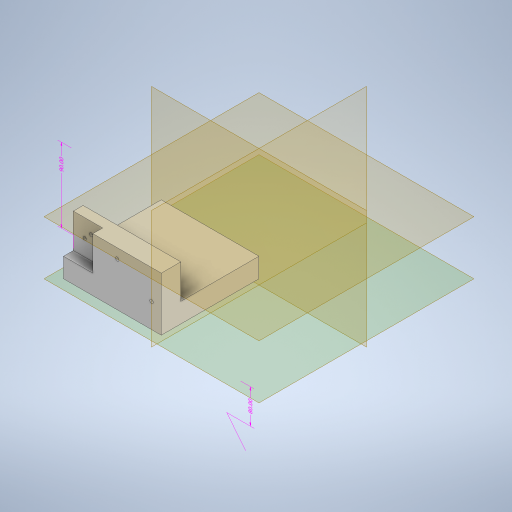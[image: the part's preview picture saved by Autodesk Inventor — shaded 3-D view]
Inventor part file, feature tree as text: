
AUTODESK INVENTOR PART (.ipt)
format: ipt  version: 2023 (Build 270158000, 158)  size: 432,128 bytes
history: native  units: mm
features: sketch x9, extrude x5, other x4, hole x4, plane x4, split x4
ambient origin geometry x8: Origin, YZ Plane, XZ Plane, XY Plane, X Axis, Y Axis, Z Axis, Center Point
bodies: Body1 (feature_tree)
feature tree (30):
  other  "Sólido1"
  other  "Anotaciones"
  extrude  "Extrusión1"  Depth=200.0mm
  hole  "Agujero1"  [1 undecoded]
  extrude  "Extrusión2"  Depth=15.0mm
  extrude  "Extrusión3"  Depth=80.0mm TaperAngle=0.0deg
  extrude  "Extrusión4"  Depth=200.0mm
  extrude  "Extrusión5"  Depth=20.0mm
  hole  "Agujero2"  [1 undecoded]
  plane  "Plano de trabajo1"
  split  "Dividir1"
  plane  "Plano de trabajo2"
  plane  "Plano de trabajo3"
  sketch  "Boceto9"  dims[d37=20.0mm d38=20.0mm]
  plane  "Plano de trabajo4"
  hole  "Agujero3"  [1 undecoded]
  hole  "Agujero4"  [1 undecoded]
  split  "Dividir2"
  split  "Dividir3"
  split  "Dividir4"
  sketch  "Boceto2"  dims[d7=15.0mm d8=200.0mm]
  sketch  "Boceto3"  dims[d9=10.0mm d10=0.0mm]
  sketch  "Boceto4"  dims[d12=1.75mm d13=1.75mm d14=1.75mm d15=1.75mm d16=10.0mm d17=10.0mm d19=30.0mm]
  sketch  "Boceto5"  dims[d20=3.5mm d21=6.0mm d22=4.0mm d23=2.0mm d24=90.0deg d25=8.0mm d26=20.594885mm d27=15.0mm]
  sketch  "Boceto6"  dims[d28=20.0mm d29=80.0mm d30=0.0mm]
  sketch  "Boceto7"  dims[d31=48.0mm d32=200.0mm]
  sketch  "Boceto8"  dims[d33=110.0mm d34=0.0mm d36=20.0mm]
  sketch  "Boceto10"  dims[d39=90.0mm d40=0.0mm d42=10.0mm d43=30.0mm d44=0.0mm d46=1.75mm d47=1.75mm d48=1.75mm d49=1.75mm d50=10.0mm d51=10.0mm d52=15.0mm d56=3.5mm d57=6.0mm d58=4.0mm d59=2.0mm d60=90.0deg d61=8.0mm d62=20.594885mm d63=10.0mm d65=10.0mm d66=10.0mm d67=31.75mm d70=15.0mm d74=200.0mm d78=20.0mm d82=90.0deg d83=10.0mm d84=30.0mm d85=5.0mm d86=5.0mm d87=5.0mm d88=5.0mm d89=20.0mm d91=30.0mm d92=5.0mm d93=5.0mm d94=3.5mm d95=5.0mm d96=5.0mm d97=5.0mm d98=5.0mm d99=5.0mm d100=20.0mm d101=3.5mm d102=6.0mm d103=4.0mm d104=2.0mm d105=90.0deg d106=8.0mm d107=20.594885mm d108=10.0mm d109=30.0mm d110=5.0mm d111=5.0mm d112=5.0mm d113=5.0mm d114=5.0mm d115=5.0mm d116=3.5mm d117=5.0mm d118=5.0mm d119=5.0mm d120=5.0mm d121=5.0mm d122=30.0mm d123=30.0mm d124=3.5mm d125=6.0mm d126=4.0mm d127=2.0mm d128=90.0deg d129=8.0mm d130=20.594885mm d75=1.454734mm d76=6.982969mm d77=80.0mm d79=4.097996mm d80=1.406125mm d81=90.0mm]
  other  "Cota lineal 2"
  other  "Cota lineal 3"
note: 4 required parameter values undecoded (feature->parameter linkage not recoverable at this tier; creation-order binding heuristic only, values carry confidence <= 0.55)
